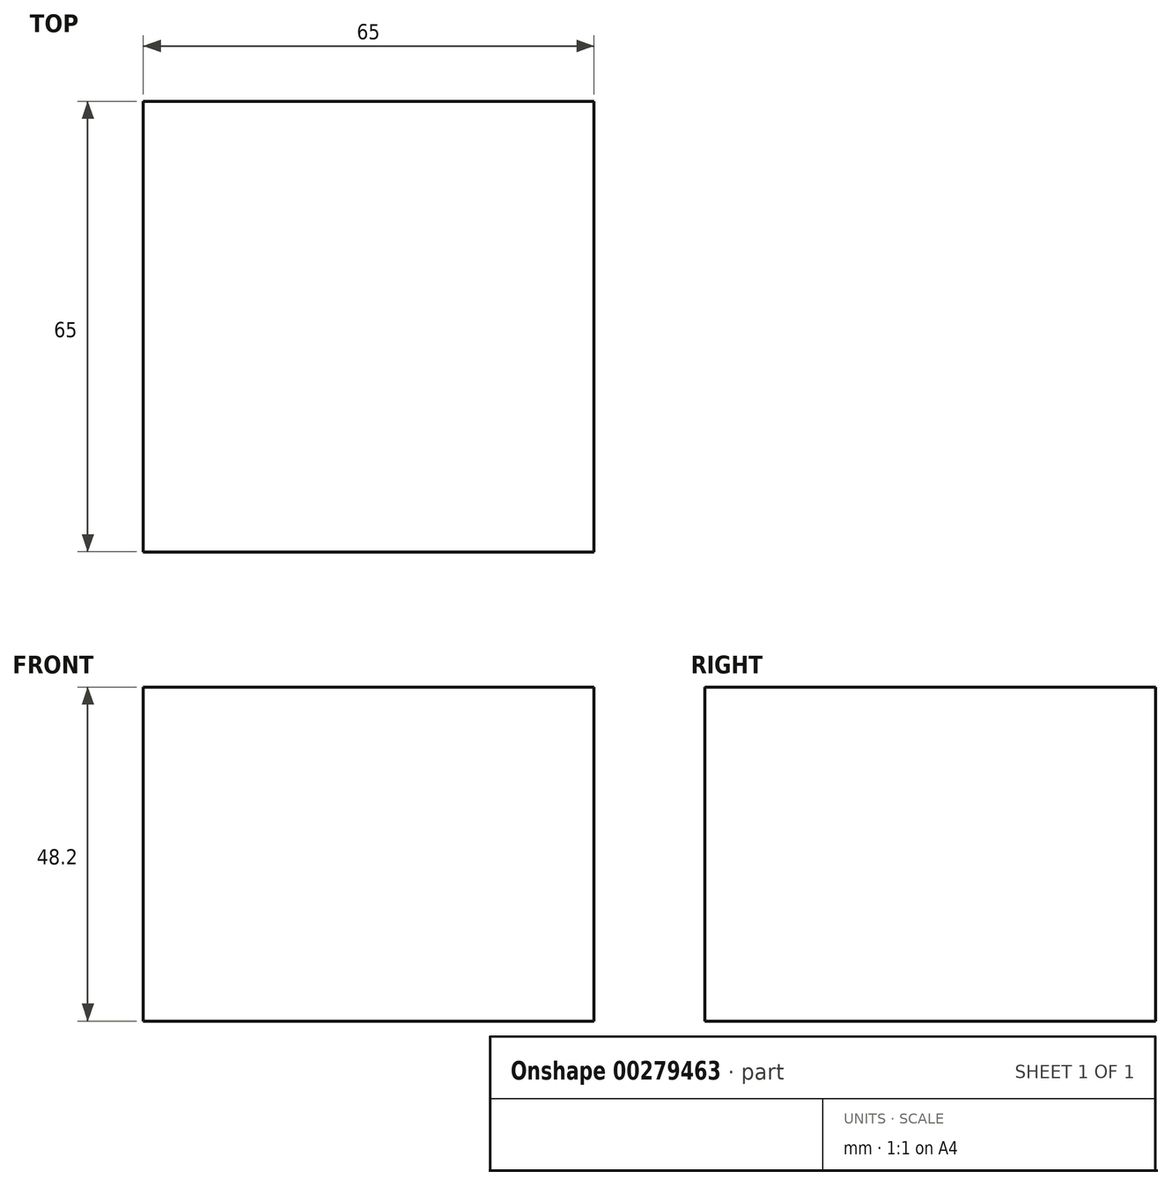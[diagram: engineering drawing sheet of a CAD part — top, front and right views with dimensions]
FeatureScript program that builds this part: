
annotation { "Feature Type Name" : "Feature", "Feature Type Description" : "" }
export const myFeature = defineFeature(function(context is Context, id is Id, definition is map)
    precondition{}
    {
        {
            var Q0;
            Q0=qCreatedBy(makeId("Top.planeOp"),FACE);
            var sketch = newSketch(context, id + "F0", { "sketchPlane" : qUnion([Q0])});
            skLineSegment(sketch, "E0.bottom", {"start": v(-33.56, 24.14) * mm, "end": v(31.44, 24.14) * mm});
            skLineSegment(sketch, "E0.top", {"start": v(-33.56, -40.86) * mm, "end": v(31.44, -40.86) * mm});
            skLineSegment(sketch, "E0.left", {"start": v(-33.56, 24.14) * mm, "end": v(-33.56, -40.86) * mm});
            skLineSegment(sketch, "E0.right", {"start": v(31.44, 24.14) * mm, "end": v(31.44, -40.86) * mm});
            skSolve(sketch);
        }
        {
            var Q0;
            Q0 = qSketchRegion(id + "F0", true);
            extrude(context, id + "F1", {"entities" : qUnion([Q0]), "depth" : 48.2 * mm});
        }
        {
            var Q0;
            Q0 = qSketchRegion(id + "F0", true);
            extrude(context, id + "F2", {"entities" : qUnion([Q0]), "operationType" : NewBodyOperationType.ADD, "depth" : 11.8 * mm});
        }
    });
